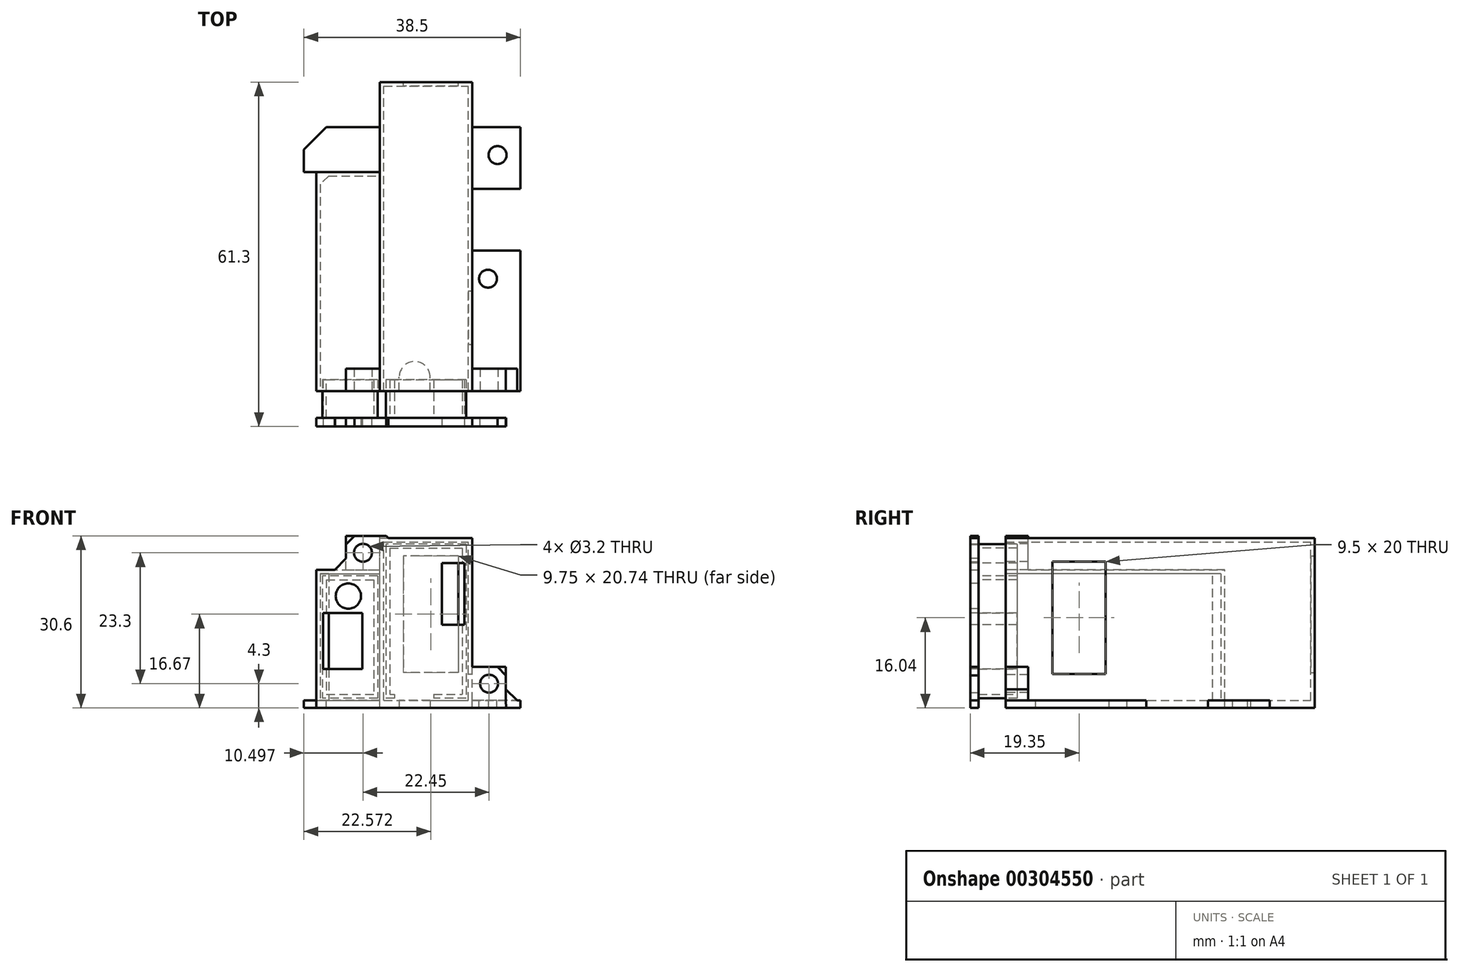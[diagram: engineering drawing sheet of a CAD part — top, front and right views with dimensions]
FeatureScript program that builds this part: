
annotation { "Feature Type Name" : "Feature", "Feature Type Description" : "" }
export const myFeature = defineFeature(function(context is Context, id is Id, definition is map)
    precondition{}
    {
        {
            var Q0;
            Q0=qCreatedBy(makeId("Front.planeOp"),FACE);
            var sketch = newSketch(context, id + "F0", { "sketchPlane" : qUnion([Q0])});
            skLineSegment(sketch, "E0.bottom", {"start": v(-5.75, 0.6) * mm, "end": v(10.7, 0.6) * mm});
            skLineSegment(sketch, "E0.top", {"start": v(-5.75, 30.24) * mm, "end": v(10.7, 30.24) * mm});
            skLineSegment(sketch, "E0.left", {"start": v(-5.75, 0.6) * mm, "end": v(-5.75, 30.24) * mm});
            skLineSegment(sketch, "E0.right", {"start": v(10.7, 0.6) * mm, "end": v(10.7, 30.24) * mm});
            skSolve(sketch);
        }
        {
            var Q0;
            Q0=makeQuery(id+"F0.imprint","IMPRINT",FACE,{"disambiguationData":[TD([[makeQuery(id+"F0.imprint","IMPRINT",EDGE,{"derivedFrom":sQuery(id+"F0.wireOp",EDGE,"E0.bottom")}),1.0]])]});
            extrude(context, id + "F1", {"entities" : qUnion([Q0]), "depth" : 55 * mm});
        }
        {
            var Q0;
            Q0=makeQuery(id+"F1.opExtrude","CAP_FACE",FACE,{"disambiguationData":[OSD([sQuery(id+"F0.wireOp",EDGE,"E0.bottom"),sQuery(id+"F0.wireOp",EDGE,"E0.top"),sQuery(id+"F0.wireOp",EDGE,"E0.left"),sQuery(id+"F0.wireOp",EDGE,"E0.right")])],"isStart":false});
            shell(context, id + "F2", {"entities" : qUnion([Q0]), "thickness" : 0.7 * mm});
        }
        {
            var Q0;
            Q0=makeQuery(id+"F1.opExtrude","CAP_FACE",FACE,{"disambiguationData":[OSD([sQuery(id+"F0.wireOp",EDGE,"E0.bottom"),sQuery(id+"F0.wireOp",EDGE,"E0.top"),sQuery(id+"F0.wireOp",EDGE,"E0.left"),sQuery(id+"F0.wireOp",EDGE,"E0.right")])],"isStart":true});
            var sketch = newSketch(context, id + "F3", { "sketchPlane" : qUnion([Q0])});
            skLineSegment(sketch, "E1.bottom", {"start": v(-8.2, 27.04) * mm, "end": v(1.55, 27.04) * mm});
            skLineSegment(sketch, "E1.top", {"start": v(-8.2, 6.3) * mm, "end": v(1.55, 6.3) * mm});
            skLineSegment(sketch, "E1.left", {"start": v(-8.2, 27.04) * mm, "end": v(-8.2, 6.3) * mm});
            skLineSegment(sketch, "E1.right", {"start": v(1.55, 27.04) * mm, "end": v(1.55, 6.3) * mm});
            skLineSegment(sketch, "E2.0.0", {"start": v(-10, 29.54) * mm, "end": v(5.05, 29.54) * mm});
            skLineSegment(sketch, "E2.0.1", {"start": v(5.05, 29.54) * mm, "end": v(5.05, 1.3) * mm});
            skLineSegment(sketch, "E2.0.2", {"start": v(5.05, 1.3) * mm, "end": v(-10, 1.3) * mm});
            skLineSegment(sketch, "E2.0.3", {"start": v(-10, 1.3) * mm, "end": v(-10, 29.54) * mm});
            skSolve(sketch);
        }
        {
            var Q0;
            Q0=makeQuery(id+"F3.imprint","IMPRINT",FACE,{"disambiguationData":[TD([[makeQuery(id+"F3.imprint","IMPRINT",EDGE,{"derivedFrom":sQuery(id+"F3.wireOp",EDGE,"E1.bottom")}),-1.0]])]});
            extrude(context, id + "F4", {"entities" : qUnion([Q0]), "operationType" : NewBodyOperationType.REMOVE, "endBound" : BoundingType.UP_TO_NEXT, "oppositeDirection" : true, "depth" : 25 * mm});
        }
        {
            var Q0;
            Q0=makeQuery(id+"F2.opShell","OFFSET_FACE",FACE,{"disambiguationData":[OSD([sQuery(id+"F0.wireOp",EDGE,"E0.left")])]});
            var sketch = newSketch(context, id + "F5", { "sketchPlane" : qUnion([Q0])});
            skLineSegment(sketch, "E3.bottom", {"start": v(-16, 24.6) * mm, "end": v(-55, 24.6) * mm});
            skLineSegment(sketch, "E3.top", {"start": v(-16, 0.6) * mm, "end": v(-55, 0.6) * mm});
            skLineSegment(sketch, "E3.left", {"start": v(-16, 24.6) * mm, "end": v(-16, 0.6) * mm});
            skLineSegment(sketch, "E3.right", {"start": v(-55, 24.6) * mm, "end": v(-55, 0.6) * mm});
            skSolve(sketch);
        }
        {
            var Q0;
            Q0 = qSketchRegion(id + "F5", true);
            extrude(context, id + "F6", {"entities" : qUnion([Q0]), "oppositeDirection" : true, "depth" : 12 * mm});
        }
        {
            var Q0;
            Q0=makeQuery(id+"F6.opExtrude","SWEPT_FACE",FACE,{"disambiguationData":[OSD([sQuery(id+"F5.wireOp",EDGE,"E3.right")])]});
            shell(context, id + "F7", {"entities" : qUnion([Q0]), "thickness" : 0.7 * mm});
        }
        {
            var Q0;
            Q0=qCreatedBy(makeId("Top.planeOp"),FACE);
            var sketch = newSketch(context, id + "F8", { "sketchPlane" : qUnion([Q0])});
            skLineSegment(sketch, "E4.bottom", {"start": v(-19.25, -55) * mm, "end": v(19.25, -55) * mm});
            skLineSegment(sketch, "E4.top", {"start": v(-19.25, 0) * mm, "end": v(19.25, 0) * mm});
            skLineSegment(sketch, "E4.left", {"start": v(-19.25, -55) * mm, "end": v(-19.25, 0) * mm});
            skLineSegment(sketch, "E4.right", {"start": v(19.25, -55) * mm, "end": v(19.25, 0) * mm});
            skPoint(sketch, "E5.0", {"position": v(-5.75, -55) * mm});
            skSolve(sketch);
        }
        {
            var Q0;
            Q0=makeQuery(id+"F8.imprint","IMPRINT",FACE,{"disambiguationData":[TD([[makeQuery(id+"F8.imprint","IMPRINT",EDGE,{"derivedFrom":sQuery(id+"F8.wireOp",EDGE,"E4.bottom")}),1.0]])]});
            extrude(context, id + "F9", {"entities" : qUnion([Q0]), "depth" : 1.3 * mm});
        }
        {
            var Q0;
            Q0=makeQuery(id+"F9.opExtrude","CAP_FACE",FACE,{"disambiguationData":[OSD([sQuery(id+"F8.wireOp",EDGE,"E4.bottom"),sQuery(id+"F8.wireOp",EDGE,"E4.top"),sQuery(id+"F8.wireOp",EDGE,"E4.left"),sQuery(id+"F8.wireOp",EDGE,"E4.right")])],"isStart":false});
            var sketch = newSketch(context, id + "F10", { "sketchPlane" : qUnion([Q0])});
            skCircle(sketch, "E6", {"center": v(15.2, -13) * mm, "radius": 1.6 * mm});
            skCircle(sketch, "E7", {"center": v(13.5, -35) * mm, "radius": 1.6 * mm});
            skSolve(sketch);
        }
        {
            var Q0;
            Q0 = qSketchRegion(id + "F10", true);
            var Q1;
            Q1=makeQuery(id+"F9.opExtrude","CAP_FACE",FACE,{"disambiguationData":[OSD([sQuery(id+"F8.wireOp",EDGE,"E4.bottom"),sQuery(id+"F8.wireOp",EDGE,"E4.top"),sQuery(id+"F8.wireOp",EDGE,"E4.left"),sQuery(id+"F8.wireOp",EDGE,"E4.right")])],"isStart":true});
            extrude(context, id + "F11", {"entities" : qUnion([Q0]), "operationType" : NewBodyOperationType.REMOVE, "endBound" : BoundingType.UP_TO_SURFACE, "oppositeDirection" : true, "endBoundEntityFace" : qUnion([Q1]), "depth" : 25 * mm});
        }
        {
            var Q0;
            Q0=makeQuery(id+"F9.opExtrude","SWEPT_EDGE",EDGE,{"disambiguationData":[OSD([sQuery(id+"F8.wireOp",EDGE,"E4.top"),sQuery(id+"F8.wireOp",EDGE,"E4.left")])]});
            chamfer(context, id + "F12", {"entities" : qUnion([Q0]), "width" : 12 * mm, "tangentPropagation" : true});
        }
        {
            var Q0;
            Q0=makeQuery(id+"F9.opExtrude","SWEPT_EDGE",EDGE,{"disambiguationData":[OSD([sQuery(id+"F8.wireOp",EDGE,"E4.top"),sQuery(id+"F8.wireOp",EDGE,"E4.right")])]});
            chamfer(context, id + "F13", {"entities" : qUnion([Q0]), "width" : 8 * mm, "tangentPropagation" : true});
        }
        {
            var Q0;
            Q0=makeQuery(id+"F6.opExtrude","SWEPT_FACE",FACE,{"disambiguationData":[OSD([sQuery(id+"F5.wireOp",EDGE,"E3.right")])]});
            var sketch = newSketch(context, id + "F14", { "sketchPlane" : qUnion([Q0])});
            skLineSegment(sketch, "E8.bottom", {"start": v(-11.75, 24.6) * mm, "end": v(-5.75, 24.6) * mm});
            skLineSegment(sketch, "E8.top", {"start": v(-11.75, 30.6) * mm, "end": v(-5.75, 30.6) * mm});
            skLineSegment(sketch, "E8.left", {"start": v(-11.75, 24.6) * mm, "end": v(-11.75, 30.6) * mm});
            skLineSegment(sketch, "E8.right", {"start": v(-5.75, 24.6) * mm, "end": v(-5.75, 30.6) * mm});
            skPoint(sketch, "E9", {"position": v(-8.75, 27.6) * mm});
            skLineSegment(sketch, "E10", {"start": v(-11.75, 27.6) * mm, "end": v(-5.75, 27.6) * mm});
            skPoint(sketch, "E11.0", {"position": v(10.7, 0.6) * mm});
            skLineSegment(sketch, "E12.bottom", {"start": v(10.7, 1.3) * mm, "end": v(16.7, 1.3) * mm});
            skLineSegment(sketch, "E12.top", {"start": v(10.7, 7.3) * mm, "end": v(16.7, 7.3) * mm});
            skLineSegment(sketch, "E12.left", {"start": v(10.7, 1.3) * mm, "end": v(10.7, 7.3) * mm});
            skLineSegment(sketch, "E12.right", {"start": v(16.7, 1.3) * mm, "end": v(16.7, 7.3) * mm});
            skLineSegment(sketch, "E13", {"start": v(10.7, 4.3) * mm, "end": v(16.7, 4.3) * mm});
            skPoint(sketch, "E14", {"position": v(13.7, 4.3) * mm});
            skCircle(sketch, "E15", {"center": v(-8.75, 27.6) * mm, "radius": 1.6 * mm});
            skCircle(sketch, "E16", {"center": v(13.7, 4.3) * mm, "radius": 1.6 * mm});
            skSolve(sketch);
        }
        {
            var Q0;
            Q0=makeQuery(id+"F14.imprint","IMPRINT",FACE,{"disambiguationData":[TD([[makeQuery(id+"F14.imprint","IMPRINT",EDGE,{"derivedFrom":sQuery(id+"F14.wireOp",EDGE,"E8.bottom")}),1.0]])]});
            var Q1;
            {var subQ0=sQuery(id+"F14.wireOp",EDGE,"E8.top");Q1=makeQuery(id+"F14.imprint","IMPRINT",FACE,{"disambiguationData":[TD([[makeQuery(id+"F14.imprint","IMPRINT",EDGE,{"derivedFrom":subQ0}),-1.0]])]});}
            var Q2;
            {var subQ0=sQuery(id+"F14.wireOp",EDGE,"E12.top");Q2=makeQuery(id+"F14.imprint","IMPRINT",FACE,{"disambiguationData":[TD([[makeQuery(id+"F14.imprint","IMPRINT",EDGE,{"derivedFrom":subQ0}),-1.0]])]});}
            var Q3;
            {var subQ0=sQuery(id+"F14.wireOp",EDGE,"E12.bottom");Q3=makeQuery(id+"F14.imprint","IMPRINT",FACE,{"disambiguationData":[TD([[makeQuery(id+"F14.imprint","IMPRINT",EDGE,{"derivedFrom":subQ0}),1.0]])]});}
            extrude(context, id + "F15", {"entities" : qUnion([Q0, Q1, Q2, Q3]), "oppositeDirection" : true, "depth" : 4 * mm});
        }
        {
            var Q0;
            Q0=makeQuery(id+"F15.opExtrude","CAP_FACE",FACE,{"disambiguationData":[OSD([sQuery(id+"F14.wireOp",EDGE,"E8.bottom"),sQuery(id+"F14.wireOp",EDGE,"E8.top"),sQuery(id+"F14.wireOp",EDGE,"E8.left"),sQuery(id+"F14.wireOp",EDGE,"E8.right")])],"isStart":true});
            var sketch = newSketch(context, id + "F16", { "sketchPlane" : qUnion([Q0])});
            skPoint(sketch, "E17.0", {"position": v(-5.75, 30.24) * mm});
            skPoint(sketch, "E18.0", {"position": v(10.7, 30.24) * mm});
            skPoint(sketch, "E19.0", {"position": v(10.7, 0.6) * mm});
            skPoint(sketch, "E20.0", {"position": v(-17.05, 0.6) * mm});
            skPoint(sketch, "E21.0", {"position": v(-17.05, 24.6) * mm});
            skPoint(sketch, "E22.0", {"position": v(-11.75, 24.6) * mm});
            skPoint(sketch, "E23.0", {"position": v(-11.75, 30.6) * mm});
            skPoint(sketch, "E24.0", {"position": v(-5.75, 30.6) * mm});
            skLineSegment(sketch, "E25", {"start": v(-17.05, 0) * mm, "end": v(-17.05, 24.6) * mm});
            skLineSegment(sketch, "E26", {"start": v(-17.05, 24.6) * mm, "end": v(-11.75, 24.6) * mm});
            skLineSegment(sketch, "E27", {"start": v(-11.75, 24.6) * mm, "end": v(-11.75, 30.6) * mm});
            skLineSegment(sketch, "E28", {"start": v(-11.75, 30.6) * mm, "end": v(-5.75, 30.6) * mm});
            skLineSegment(sketch, "E29", {"start": v(-5.75, 30.6) * mm, "end": v(-5.75, 30.24) * mm});
            skLineSegment(sketch, "E30", {"start": v(-5.75, 30.24) * mm, "end": v(10.7, 30.24) * mm});
            skLineSegment(sketch, "E31", {"start": v(16.72, 0) * mm, "end": v(-17.05, 0) * mm});
            skPoint(sketch, "E32.0", {"position": v(10.7, 7.3) * mm});
            skPoint(sketch, "E33.0", {"position": v(16.7, 1.3) * mm});
            skLineSegment(sketch, "E34", {"start": v(10.7, 30.24) * mm, "end": v(10.7, 7.3) * mm});
            skLineSegment(sketch, "E35", {"start": v(16.72, 0) * mm, "end": v(16.7, 1.3) * mm});
            skLineSegment(sketch, "E36", {"start": v(16.7, 1.3) * mm, "end": v(10.7, 1.3) * mm});
            skLineSegment(sketch, "E37", {"start": v(10.7, 1.3) * mm, "end": v(10.7, 7.3) * mm});
            skSolve(sketch);
        }
        {
            var Q0;
            Q0=makeQuery(id+"F16.imprint","IMPRINT",FACE,{"disambiguationData":[TD([[makeQuery(id+"F16.imprint","IMPRINT",EDGE,{"derivedFrom":sQuery(id+"F16.wireOp",EDGE,"E25")}),-1.0]])]});
            var Q1;
            Q1=makeQuery(id+"F16.imprint","IMPRINT",FACE,{"disambiguationData":[TD([[makeQuery(id+"F16.imprint","IMPRINT",EDGE,{"derivedFrom":sQuery(id+"F16.wireOp",EDGE,"E27")}),-1.0]])]});
            var Q2;
            Q2=makeQuery(id+"F15.opExtrude","CAP_FACE",FACE,{"disambiguationData":[OSD([sQuery(id+"F14.wireOp",EDGE,"E12.bottom"),sQuery(id+"F14.wireOp",EDGE,"E12.top"),sQuery(id+"F14.wireOp",EDGE,"E12.left"),sQuery(id+"F14.wireOp",EDGE,"E12.right"),sQuery(id+"F14.wireOp",EDGE,"E16")])],"isStart":true});
            extrude(context, id + "F17", {"entities" : qUnion([Q0, Q1, Q2]), "depth" : 1.5 * mm});
        }
        {
            var Q0;
            Q0=makeQuery(id+"F17.opExtrude","CAP_FACE",FACE,{"disambiguationData":[OSD([sQuery(id+"F16.wireOp",EDGE,"E25"),sQuery(id+"F16.wireOp",EDGE,"E26"),sQuery(id+"F16.wireOp",EDGE,"E27"),sQuery(id+"F16.wireOp",EDGE,"E28"),sQuery(id+"F16.wireOp",EDGE,"E29"),sQuery(id+"F16.wireOp",EDGE,"E30"),sQuery(id+"F16.wireOp",EDGE,"dLR5ZEAd-W9p6-nn1V-uw1r-p6ehXEuAr7GT"),sQuery(id+"F16.wireOp",EDGE,"E31")])],"isStart":true});
            var sketch = newSketch(context, id + "F18", { "sketchPlane" : qUnion([Q0])});
            skPoint(sketch, "E38.0", {"position": v(16.35, 23.9) * mm});
            skPoint(sketch, "E39.0", {"position": v(5.75, 23.9) * mm});
            skPoint(sketch, "E40.0", {"position": v(5.75, 1.3) * mm});
            skPoint(sketch, "E41.0", {"position": v(16.35, 1.3) * mm});
            skPoint(sketch, "E42.0", {"position": v(5.05, 1.3) * mm});
            skPoint(sketch, "E43.0", {"position": v(-10, 1.3) * mm});
            skPoint(sketch, "E44.0", {"position": v(5.05, 29.54) * mm});
            skPoint(sketch, "E45.0", {"position": v(-10, 29.54) * mm});
            skLineSegment(sketch, "E46.bottom", {"start": v(-9.6, 29.14) * mm, "end": v(4.65, 29.14) * mm});
            skLineSegment(sketch, "E46.top", {"start": v(-9.6, 1.7) * mm, "end": v(4.65, 1.7) * mm});
            skLineSegment(sketch, "E46.left", {"start": v(-9.6, 29.14) * mm, "end": v(-9.6, 1.7) * mm});
            skLineSegment(sketch, "E46.right", {"start": v(4.65, 29.14) * mm, "end": v(4.65, 1.7) * mm});
            skLineSegment(sketch, "E47.bottom", {"start": v(6.15, 23.5) * mm, "end": v(15.95, 23.5) * mm});
            skLineSegment(sketch, "E47.top", {"start": v(6.15, 1.7) * mm, "end": v(15.95, 1.7) * mm});
            skLineSegment(sketch, "E47.left", {"start": v(6.15, 23.5) * mm, "end": v(6.15, 1.7) * mm});
            skLineSegment(sketch, "E47.right", {"start": v(15.95, 23.5) * mm, "end": v(15.95, 1.7) * mm});
            skLineSegment(sketch, "E48.bottom", {"start": v(15.25, 22.8) * mm, "end": v(6.85, 22.8) * mm});
            skLineSegment(sketch, "E48.top", {"start": v(15.25, 2.4) * mm, "end": v(6.85, 2.4) * mm});
            skLineSegment(sketch, "E48.left", {"start": v(15.25, 22.8) * mm, "end": v(15.25, 2.4) * mm});
            skLineSegment(sketch, "E48.right", {"start": v(6.85, 22.8) * mm, "end": v(6.85, 2.4) * mm});
            skLineSegment(sketch, "E49.bottom", {"start": v(3.95, 28.44) * mm, "end": v(-8.9, 28.44) * mm});
            skLineSegment(sketch, "E49.top", {"start": v(3.95, 2.4) * mm, "end": v(-8.9, 2.4) * mm});
            skLineSegment(sketch, "E49.left", {"start": v(3.95, 28.44) * mm, "end": v(3.95, 2.4) * mm});
            skLineSegment(sketch, "E49.right", {"start": v(-8.9, 28.44) * mm, "end": v(-8.9, 2.4) * mm});
            skSolve(sketch);
        }
        {
            var Q0;
            Q0=makeQuery(id+"F18.imprint","IMPRINT",FACE,{"disambiguationData":[TD([[makeQuery(id+"F18.imprint","IMPRINT",EDGE,{"derivedFrom":sQuery(id+"F18.wireOp",EDGE,"E46.bottom")}),-1.0]])]});
            var Q1;
            Q1=makeQuery(id+"F18.imprint","IMPRINT",FACE,{"disambiguationData":[TD([[makeQuery(id+"F18.imprint","IMPRINT",EDGE,{"derivedFrom":sQuery(id+"F18.wireOp",EDGE,"E47.bottom")}),-1.0]])]});
            extrude(context, id + "F19", {"entities" : qUnion([Q0, Q1]), "operationType" : NewBodyOperationType.ADD, "depth" : 6.8 * mm});
        }
        {
            var Q0;
            Q0=makeQuery(id+"F17.opExtrude","SWEPT_BODY",BODY,{"disambiguationData":[OSD([sQuery(id+"F14.wireOp",EDGE,"E12.bottom"),sQuery(id+"F14.wireOp",EDGE,"E12.top"),sQuery(id+"F14.wireOp",EDGE,"E12.left"),sQuery(id+"F14.wireOp",EDGE,"E12.right"),sQuery(id+"F14.wireOp",EDGE,"E16")])]});
            var Q1;
            Q1=makeQuery(id+"F17.opExtrude","SWEPT_BODY",BODY,{"disambiguationData":[OSD([sQuery(id+"F14.wireOp",EDGE,"E15"),sQuery(id+"F16.wireOp",EDGE,"E25"),sQuery(id+"F16.wireOp",EDGE,"E26"),sQuery(id+"F16.wireOp",EDGE,"E27"),sQuery(id+"F16.wireOp",EDGE,"E28"),sQuery(id+"F16.wireOp",EDGE,"E29"),sQuery(id+"F16.wireOp",EDGE,"E30"),sQuery(id+"F16.wireOp",EDGE,"E31"),sQuery(id+"F16.wireOp",EDGE,"E34"),sQuery(id+"F16.wireOp",EDGE,"QFazLDCa-6nAL-WsGP-17c7-o35cEx2jxHVR"),sQuery(id+"F16.wireOp",EDGE,"E35"),sQuery(id+"F16.wireOp",EDGE,"E36"),sQuery(id+"F16.wireOp",EDGE,"E37")])]});
            booleanBodies(context, id + "F20", {"operationType" : BooleanOperationType.UNION, "tools" : qUnion([Q0, Q1])});
        }
        {
            var Q0;
            Q0=makeQuery(id+"F17.opExtrude","SWEPT_BODY",BODY,{"disambiguationData":[OSD([sQuery(id+"F14.wireOp",EDGE,"E12.bottom"),sQuery(id+"F14.wireOp",EDGE,"E12.top"),sQuery(id+"F14.wireOp",EDGE,"E12.left"),sQuery(id+"F14.wireOp",EDGE,"E12.right"),sQuery(id+"F14.wireOp",EDGE,"E16")])]});
            transform(context, id + "F21", {"entities" : qUnion([Q0]), "transformType" : TransformType.TRANSLATION_3D, "dx" : 0 * mm, "dy" : -20 * mm, "dz" : 0 * mm, "makeCopy" : false});
        }
        {
            var Q0;
            Q0=makeQuery(id+"F20.opBoolean","MERGE",FACE,{"derivedFrom":[makeQuery(id+"F17.opExtrude","CAP_FACE",FACE,{"disambiguationData":[OSD([sQuery(id+"F14.wireOp",EDGE,"E12.bottom"),sQuery(id+"F14.wireOp",EDGE,"E12.top"),sQuery(id+"F14.wireOp",EDGE,"E12.left"),sQuery(id+"F14.wireOp",EDGE,"E12.right"),sQuery(id+"F14.wireOp",EDGE,"E16")])],"isStart":false}),makeQuery(id+"F17.opExtrude","CAP_FACE",FACE,{"disambiguationData":[OSD([sQuery(id+"F14.wireOp",EDGE,"E15"),sQuery(id+"F16.wireOp",EDGE,"E25"),sQuery(id+"F16.wireOp",EDGE,"E26"),sQuery(id+"F16.wireOp",EDGE,"E27"),sQuery(id+"F16.wireOp",EDGE,"E28"),sQuery(id+"F16.wireOp",EDGE,"E29"),sQuery(id+"F16.wireOp",EDGE,"E30"),sQuery(id+"F16.wireOp",EDGE,"E31"),sQuery(id+"F16.wireOp",EDGE,"E34"),sQuery(id+"F16.wireOp",EDGE,"QFazLDCa-6nAL-WsGP-17c7-o35cEx2jxHVR"),sQuery(id+"F16.wireOp",EDGE,"E35"),sQuery(id+"F16.wireOp",EDGE,"E36"),sQuery(id+"F16.wireOp",EDGE,"E37")])],"isStart":false})]});
            var sketch = newSketch(context, id + "F22", { "sketchPlane" : qUnion([Q0])});
            skLineSegment(sketch, "E50.bottom", {"start": v(-15.85, 6.9) * mm, "end": v(-8.85, 6.9) * mm});
            skLineSegment(sketch, "E50.top", {"start": v(-15.85, 16.9) * mm, "end": v(-8.85, 16.9) * mm});
            skLineSegment(sketch, "E50.left", {"start": v(-15.85, 6.9) * mm, "end": v(-15.85, 16.9) * mm});
            skLineSegment(sketch, "E50.right", {"start": v(-8.85, 6.9) * mm, "end": v(-8.85, 16.9) * mm});
            skCircle(sketch, "E51", {"center": v(-11.35, 19.9) * mm, "radius": 2.25 * mm});
            skPoint(sketch, "E52.0", {"position": v(-16.35, 23.9) * mm});
            skPoint(sketch, "E53.0", {"position": v(-16.35, 1.3) * mm});
            skPoint(sketch, "E54.0", {"position": v(-5.75, 23.9) * mm});
            skPoint(sketch, "E55.0", {"position": v(-5.05, 29.54) * mm});
            skPoint(sketch, "E56.0", {"position": v(10, 29.54) * mm});
            skPoint(sketch, "E57.0", {"position": v(-5.75, 1.3) * mm});
            skPoint(sketch, "E58.0", {"position": v(-5.05, 1.3) * mm});
            skPoint(sketch, "E59.0", {"position": v(10, 1.3) * mm});
            skPoint(sketch, "E60", {"position": v(-12.35, 16.9) * mm});
            skLineSegment(sketch, "E61.bottom", {"start": v(9.3, 25.79) * mm, "end": v(5.3, 25.79) * mm});
            skLineSegment(sketch, "E61.top", {"start": v(9.3, 14.79) * mm, "end": v(5.3, 14.79) * mm});
            skLineSegment(sketch, "E61.left", {"start": v(9.3, 25.79) * mm, "end": v(9.3, 14.79) * mm});
            skLineSegment(sketch, "E61.right", {"start": v(5.3, 25.79) * mm, "end": v(5.3, 14.79) * mm});
            skSolve(sketch);
        }
        {
            var Q0;
            Q0=makeQuery(id+"F22.imprint","IMPRINT",FACE,{"disambiguationData":[TD([[makeQuery(id+"F22.imprint","IMPRINT",EDGE,{"derivedFrom":sQuery(id+"F22.wireOp",EDGE,"E51")}),1.0]])]});
            var Q1;
            Q1=makeQuery(id+"F22.imprint","IMPRINT",FACE,{"disambiguationData":[TD([[makeQuery(id+"F22.imprint","IMPRINT",EDGE,{"derivedFrom":sQuery(id+"F22.wireOp",EDGE,"E50.bottom")}),1.0]])]});
            var Q2;
            Q2=makeQuery(id+"F22.imprint","IMPRINT",FACE,{"disambiguationData":[TD([[makeQuery(id+"F22.imprint","IMPRINT",EDGE,{"derivedFrom":sQuery(id+"F22.wireOp",EDGE,"E61.bottom")}),1.0]])]});
            extrude(context, id + "F23", {"entities" : qUnion([Q0, Q1, Q2]), "operationType" : NewBodyOperationType.REMOVE, "endBound" : BoundingType.UP_TO_NEXT, "oppositeDirection" : true, "depth" : 25 * mm});
        }
        {
            var Q0;
            Q0=makeQuery(id+"F1.opExtrude","SWEPT_FACE",FACE,{"disambiguationData":[OSD([sQuery(id+"F0.wireOp",EDGE,"E0.right")])]});
            var sketch = newSketch(context, id + "F24", { "sketchPlane" : qUnion([Q0])});
            skLineSegment(sketch, "E62.bottom", {"start": v(-37.2, 6.04) * mm, "end": v(-46.7, 6.04) * mm});
            skLineSegment(sketch, "E62.top", {"start": v(-37.2, 26.04) * mm, "end": v(-46.7, 26.04) * mm});
            skLineSegment(sketch, "E62.left", {"start": v(-37.2, 6.04) * mm, "end": v(-37.2, 26.04) * mm});
            skLineSegment(sketch, "E62.right", {"start": v(-46.7, 6.04) * mm, "end": v(-46.7, 26.04) * mm});
            skSolve(sketch);
        }
        {
            var Q0;
            Q0=makeQuery(id+"F24.imprint","IMPRINT",FACE,{"disambiguationData":[TD([[makeQuery(id+"F24.imprint","IMPRINT",EDGE,{"derivedFrom":sQuery(id+"F24.wireOp",EDGE,"E62.bottom")}),-1.0]])]});
            extrude(context, id + "F25", {"entities" : qUnion([Q0]), "operationType" : NewBodyOperationType.REMOVE, "endBound" : BoundingType.UP_TO_NEXT, "oppositeDirection" : true, "depth" : 25 * mm});
        }
        {
            var Q0;
            Q0=makeQuery(id+"F17.opExtrude","SWEPT_BODY",BODY,{"disambiguationData":[OSD([sQuery(id+"F14.wireOp",EDGE,"E12.bottom"),sQuery(id+"F14.wireOp",EDGE,"E12.top"),sQuery(id+"F14.wireOp",EDGE,"E12.left"),sQuery(id+"F14.wireOp",EDGE,"E12.right"),sQuery(id+"F14.wireOp",EDGE,"E16")])]});
            transform(context, id + "F26", {"entities" : qUnion([Q0]), "transformType" : TransformType.TRANSLATION_3D, "dx" : 0 * mm, "dy" : 15.2 * mm, "dz" : 0 * mm, "makeCopy" : false});
        }
        {
            var Q0;
            Q0=makeQuery(id+"F9.opExtrude","CAP_FACE",FACE,{"disambiguationData":[OSD([sQuery(id+"F8.wireOp",EDGE,"E4.bottom"),sQuery(id+"F8.wireOp",EDGE,"E4.top"),sQuery(id+"F8.wireOp",EDGE,"E4.left"),sQuery(id+"F8.wireOp",EDGE,"E4.right")])],"isStart":true});
            var sketch = newSketch(context, id + "F27", { "sketchPlane" : qUnion([Q0])});
            skLineSegment(sketch, "E63", {"start": v(-2.3, 55) * mm, "end": v(3.2, 55) * mm});
            skLineSegment(sketch, "E64", {"start": v(3.2, 55) * mm, "end": v(3.2, 52.5) * mm});
            skLineSegment(sketch, "E65", {"start": v(-2.3, 55) * mm, "end": v(-2.3, 52.5) * mm});
            skArc(sketch, "E66", {"start": v(-2.3, 52.5) * mm, "mid": v(0.45, 49.75) * mm, "end": v(3.2, 52.5) * mm});
            skPoint(sketch, "E67.0", {"position": v(-5.05, 55) * mm});
            skPoint(sketch, "E68", {"position": v(0.45, 55) * mm});
            skSolve(sketch);
        }
        {
            var Q0;
            Q0=makeQuery(id+"F27.imprint","IMPRINT",FACE,{"disambiguationData":[TD([[makeQuery(id+"F27.imprint","IMPRINT",EDGE,{"derivedFrom":sQuery(id+"F27.wireOp",EDGE,"E63")}),-1.0]])]});
            extrude(context, id + "F28", {"entities" : qUnion([Q0]), "oppositeDirection" : true, "depth" : 5 * mm});
        }
        {
            var Q0;
            Q0=makeQuery(id+"F1.opExtrude","SWEPT_BODY",BODY,{"disambiguationData":[OSD([sQuery(id+"F0.wireOp",EDGE,"E0.bottom"),sQuery(id+"F0.wireOp",EDGE,"E0.top"),sQuery(id+"F0.wireOp",EDGE,"E0.left"),sQuery(id+"F0.wireOp",EDGE,"E0.right")])]});
            var Q1;
            Q1=makeQuery(id+"F6.opExtrude","SWEPT_BODY",BODY,{"disambiguationData":[OSD([sQuery(id+"F5.wireOp",EDGE,"E3.bottom"),sQuery(id+"F5.wireOp",EDGE,"E3.top"),sQuery(id+"F5.wireOp",EDGE,"E3.left"),sQuery(id+"F5.wireOp",EDGE,"E3.right")])]});
            var Q2;
            Q2=makeQuery(id+"F9.opExtrude","SWEPT_BODY",BODY,{"disambiguationData":[OSD([sQuery(id+"F8.wireOp",EDGE,"E4.bottom"),sQuery(id+"F8.wireOp",EDGE,"E4.top"),sQuery(id+"F8.wireOp",EDGE,"E4.left"),sQuery(id+"F8.wireOp",EDGE,"E4.right")])]});
            var Q3;
            Q3=makeQuery(id+"F15.opExtrude","SWEPT_BODY",BODY,{"disambiguationData":[OSD([sQuery(id+"F14.wireOp",EDGE,"E8.bottom"),sQuery(id+"F14.wireOp",EDGE,"E8.top"),sQuery(id+"F14.wireOp",EDGE,"E8.left"),sQuery(id+"F14.wireOp",EDGE,"E8.right"),sQuery(id+"F14.wireOp",EDGE,"E15")])]});
            var Q4;
            Q4=makeQuery(id+"F15.opExtrude","SWEPT_BODY",BODY,{"disambiguationData":[OSD([sQuery(id+"F14.wireOp",EDGE,"E12.bottom"),sQuery(id+"F14.wireOp",EDGE,"E12.top"),sQuery(id+"F14.wireOp",EDGE,"E12.left"),sQuery(id+"F14.wireOp",EDGE,"E12.right"),sQuery(id+"F14.wireOp",EDGE,"E16")])]});
            booleanBodies(context, id + "F29", {"operationType" : BooleanOperationType.UNION, "tools" : qUnion([Q0, Q1, Q2, Q3, Q4])});
        }
        {
            var Q0;
            Q0=makeQuery(id+"F28.opExtrude","SWEPT_BODY",BODY,{"disambiguationData":[OSD([sQuery(id+"F27.wireOp",EDGE,"E63"),sQuery(id+"F27.wireOp",EDGE,"E64"),sQuery(id+"F27.wireOp",EDGE,"E65"),sQuery(id+"F27.wireOp",EDGE,"E66")])]});
            var Q1;
            Q1=makeQuery(id+"F1.opExtrude","SWEPT_BODY",BODY,{"disambiguationData":[OSD([sQuery(id+"F0.wireOp",EDGE,"E0.bottom"),sQuery(id+"F0.wireOp",EDGE,"E0.top"),sQuery(id+"F0.wireOp",EDGE,"E0.left"),sQuery(id+"F0.wireOp",EDGE,"E0.right")])]});
            booleanBodies(context, id + "F30", {"operationType" : BooleanOperationType.SUBTRACTION, "tools" : qUnion([Q0]), "targets" : qUnion([Q1])});
        }
        {
            var Q0;
            Q0=makeQuery(id+"F19.opExtrude","SWEPT_FACE",FACE,{"disambiguationData":[OSD([sQuery(id+"F18.wireOp",EDGE,"E46.top")])]});
            var sketch = newSketch(context, id + "F31", { "sketchPlane" : qUnion([Q0])});
            skLineSegment(sketch, "E69.bottom", {"start": v(-3.15, 53) * mm, "end": v(3.85, 53) * mm});
            skLineSegment(sketch, "E69.top", {"start": v(-3.15, 59.8) * mm, "end": v(3.85, 59.8) * mm});
            skLineSegment(sketch, "E69.left", {"start": v(-3.15, 53) * mm, "end": v(-3.15, 59.8) * mm});
            skLineSegment(sketch, "E69.right", {"start": v(3.85, 53) * mm, "end": v(3.85, 59.8) * mm});
            skSolve(sketch);
        }
        {
            var Q0;
            Q0=makeQuery(id+"F31.imprint","IMPRINT",FACE,{"disambiguationData":[TD([[makeQuery(id+"F31.imprint","IMPRINT",EDGE,{"derivedFrom":sQuery(id+"F31.wireOp",EDGE,"E69.bottom")}),-1.0]])]});
            extrude(context, id + "F32", {"entities" : qUnion([Q0]), "operationType" : NewBodyOperationType.REMOVE, "endBound" : BoundingType.UP_TO_NEXT, "oppositeDirection" : true, "depth" : 25 * mm});
        }
        {
            var Q0;
            Q0=makeQuery(id+"F15.opExtrude","SWEPT_EDGE",EDGE,{"disambiguationData":[OSD([sQuery(id+"F14.wireOp",EDGE,"E12.top"),sQuery(id+"F14.wireOp",EDGE,"E12.left")])]});
            var Q1;
            Q1=makeQuery(id+"F15.opExtrude","SWEPT_EDGE",EDGE,{"disambiguationData":[OSD([sQuery(id+"F14.wireOp",EDGE,"E12.bottom"),sQuery(id+"F14.wireOp",EDGE,"E12.right")])]});
            var Q2;
            Q2=makeQuery(id+"F15.opExtrude","SWEPT_EDGE",EDGE,{"disambiguationData":[OSD([sQuery(id+"F0.wireOp",EDGE,"E0.left"),sQuery(id+"F5.wireOp",EDGE,"E3.bottom"),sQuery(id+"F5.wireOp",EDGE,"E3.right"),sQuery(id+"F14.wireOp",EDGE,"E8.bottom"),sQuery(id+"F14.wireOp",EDGE,"E8.left")])]});
            var Q3;
            Q3=makeQuery(id+"F17.opExtrude","SWEPT_EDGE",EDGE,{"disambiguationData":[OSD([sQuery(id+"F14.wireOp",EDGE,"E12.top"),sQuery(id+"F14.wireOp",EDGE,"E12.left")])]});
            var Q4;
            Q4=makeQuery(id+"F17.opExtrude","SWEPT_EDGE",EDGE,{"disambiguationData":[OSD([sQuery(id+"F14.wireOp",EDGE,"E8.bottom"),sQuery(id+"F16.wireOp",EDGE,"E26"),sQuery(id+"F16.wireOp",EDGE,"E27")])]});
            chamfer(context, id + "F33", {"entities" : qUnion([Q0, Q1, Q2, Q3, Q4]), "width" : 2 * mm, "tangentPropagation" : true});
        }
        {
            var Q0;
            {var subQ0=sQuery(id+"F8.wireOp",EDGE,"E4.right");var subQ1=sQuery(id+"F8.wireOp",EDGE,"E4.top");var subQ7=sQuery(id+"F0.wireOp",EDGE,"E0.right");var subQ11=sQuery(id+"F8.wireOp",EDGE,"E4.bottom");Q0=makeQuery(id+"F29.opBoolean","SPLIT",FACE,{"disambiguationData":[TD([makeQuery(id+"F1.opExtrude","SWEPT_FACE",FACE,{"disambiguationData":[OSD([subQ7])]})])],"derivedFrom":makeQuery(id+"F9.opExtrude","CAP_FACE",FACE,{"disambiguationData":[OSD([subQ11,subQ1,sQuery(id+"F8.wireOp",EDGE,"E4.left"),subQ0])],"isStart":false})});}
            var sketch = newSketch(context, id + "F34", { "sketchPlane" : qUnion([Q0])});
            skLineSegment(sketch, "E70.bottom", {"start": v(19.25, -19) * mm, "end": v(10.7, -19) * mm});
            skLineSegment(sketch, "E70.top", {"start": v(19.25, -30) * mm, "end": v(10.7, -30) * mm});
            skLineSegment(sketch, "E70.left", {"start": v(19.25, -19) * mm, "end": v(19.25, -30) * mm});
            skLineSegment(sketch, "E70.right", {"start": v(10.7, -19) * mm, "end": v(10.7, -30) * mm});
            skLineSegment(sketch, "E71.bottom", {"start": v(19.25, -8) * mm, "end": v(10.7, -8) * mm});
            skLineSegment(sketch, "E71.top", {"start": v(19.25, 0) * mm, "end": v(10.7, 0) * mm});
            skLineSegment(sketch, "E71.left", {"start": v(19.25, -8) * mm, "end": v(19.25, 0) * mm});
            skLineSegment(sketch, "E71.right", {"start": v(10.7, -8) * mm, "end": v(10.7, 0) * mm});
            skLineSegment(sketch, "E72.bottom", {"start": v(-5.75, 0) * mm, "end": v(-19.75, 0) * mm});
            skLineSegment(sketch, "E72.top", {"start": v(-5.75, -8) * mm, "end": v(-19.75, -8) * mm});
            skLineSegment(sketch, "E72.left", {"start": v(-5.75, 0) * mm, "end": v(-5.75, -8) * mm});
            skLineSegment(sketch, "E72.right", {"start": v(-19.75, 0) * mm, "end": v(-19.75, -8) * mm});
            skPoint(sketch, "E73.0", {"position": v(-19.25, -55) * mm});
            skPoint(sketch, "E74.0", {"position": v(-17.05, -16) * mm});
            skLineSegment(sketch, "E75.bottom", {"start": v(-19.25, -55) * mm, "end": v(-17.05, -55) * mm});
            skLineSegment(sketch, "E75.top", {"start": v(-19.25, -16) * mm, "end": v(-17.05, -16) * mm});
            skLineSegment(sketch, "E75.left", {"start": v(-19.25, -55) * mm, "end": v(-19.25, -16) * mm});
            skLineSegment(sketch, "E75.right", {"start": v(-17.05, -55) * mm, "end": v(-17.05, -16) * mm});
            skSolve(sketch);
        }
        {
            var Q0;
            Q0=makeQuery(id+"F34.imprint","IMPRINT",FACE,{"disambiguationData":[TD([[makeQuery(id+"F34.imprint","IMPRINT",EDGE,{"derivedFrom":sQuery(id+"F34.wireOp",EDGE,"E72.bottom")}),1.0]])]});
            var Q1;
            {var subQ4=sQuery(id+"F34.wireOp",EDGE,"E71.left");Q1=makeQuery(id+"F34.imprint","IMPRINT",FACE,{"disambiguationData":[TD([[makeQuery(id+"F34.imprint","IMPRINT",EDGE,{"derivedFrom":subQ4}),1.0]])]});}
            var Q2;
            Q2=makeQuery(id+"F34.imprint","IMPRINT",FACE,{"disambiguationData":[TD([[makeQuery(id+"F34.imprint","IMPRINT",EDGE,{"derivedFrom":sQuery(id+"F34.wireOp",EDGE,"E71.bottom")}),-1.0]])]});
            var Q3;
            Q3=makeQuery(id+"F34.imprint","IMPRINT",FACE,{"disambiguationData":[TD([[makeQuery(id+"F34.imprint","IMPRINT",EDGE,{"derivedFrom":sQuery(id+"F34.wireOp",EDGE,"E70.bottom")}),1.0]])]});
            var Q4;
            Q4=makeQuery(id+"F34.imprint","IMPRINT",FACE,{"disambiguationData":[TD([[makeQuery(id+"F34.imprint","IMPRINT",EDGE,{"derivedFrom":sQuery(id+"F34.wireOp",EDGE,"E75.bottom")}),1.0]])]});
            extrude(context, id + "F35", {"entities" : qUnion([Q0, Q1, Q2, Q3, Q4]), "operationType" : NewBodyOperationType.REMOVE, "endBound" : BoundingType.THROUGH_ALL, "oppositeDirection" : true, "depth" : 25 * mm});
        }
        {
            var Q0;
            {var subQ0=makeQuery(id+"F1.opExtrude","SWEPT_FACE",FACE,{"disambiguationData":[OSD([sQuery(id+"F0.wireOp",EDGE,"E0.left")])]});var subQ1=makeQuery(id+"F9.opExtrude","CAP_FACE",FACE,{"disambiguationData":[OSD([sQuery(id+"F8.wireOp",EDGE,"E4.bottom"),sQuery(id+"F8.wireOp",EDGE,"E4.top"),sQuery(id+"F8.wireOp",EDGE,"E4.left"),sQuery(id+"F8.wireOp",EDGE,"E4.right")])],"isStart":false});Q0=makeQuery(id+"F29.opBoolean","INTERSECT",EDGE,{"disambiguationData":[topologyDisambiguationEdgeConnected([subQ1])],"derivedFrom":[subQ0,subQ1]});}
            var Q1;
            Q1=makeQuery(id+"F35.boolean.opBoolean","COPY",EDGE,{"derivedFrom":makeQuery(id+"F35.opExtrude","SWEPT_EDGE",EDGE,{"disambiguationData":[OSD([sQuery(id+"F34.wireOp",EDGE,"E75.top"),sQuery(id+"F34.wireOp",EDGE,"E75.left")])]})});
            var Q2;
            Q2=makeQuery(id+"F35.boolean.opBoolean","COPY",EDGE,{"derivedFrom":makeQuery(id+"F35.opExtrude","SWEPT_EDGE",EDGE,{"disambiguationData":[OSD([sQuery(id+"F0.wireOp",EDGE,"E0.right"),sQuery(id+"F8.wireOp",EDGE,"E4.bottom"),sQuery(id+"F8.wireOp",EDGE,"E4.top"),sQuery(id+"F8.wireOp",EDGE,"E4.left"),sQuery(id+"F8.wireOp",EDGE,"E4.right"),sQuery(id+"F34.wireOp",EDGE,"E71.bottom"),sQuery(id+"F34.wireOp",EDGE,"E71.right")])]})});
            var Q3;
            {var subQ0=sQuery(id+"F8.wireOp",EDGE,"E4.right");var subQ1=sQuery(id+"F8.wireOp",EDGE,"E4.top");Q3=makeQuery(id+"F35.boolean.opBoolean","MERGE",EDGE,{"derivedFrom":[makeQuery(id+"F13.opChamfer","BLEND_EDGE",EDGE,{"blendedFrom":[makeQuery(id+"F9.opExtrude","SWEPT_EDGE",EDGE,{"disambiguationData":[OSD([subQ1,subQ0])]}),makeQuery(id+"F9.opExtrude","SWEPT_FACE",FACE,{"disambiguationData":[OSD([subQ0])]})],"blendedInto":[makeQuery(id+"F9.opExtrude","SWEPT_FACE",FACE,{"disambiguationData":[OSD([subQ0])]})]}),makeQuery(id+"F35.opExtrude","SWEPT_EDGE",EDGE,{"disambiguationData":[OSD([sQuery(id+"F8.wireOp",EDGE,"E4.bottom"),subQ1,sQuery(id+"F8.wireOp",EDGE,"E4.left"),subQ0,sQuery(id+"F34.wireOp",EDGE,"E71.bottom"),sQuery(id+"F34.wireOp",EDGE,"E71.left")])]})]});}
            var Q4;
            Q4=makeQuery(id+"F35.boolean.opBoolean","COPY",EDGE,{"derivedFrom":makeQuery(id+"F35.opExtrude","SWEPT_EDGE",EDGE,{"disambiguationData":[OSD([sQuery(id+"F8.wireOp",EDGE,"E4.right"),sQuery(id+"F34.wireOp",EDGE,"E70.bottom"),sQuery(id+"F34.wireOp",EDGE,"E70.left")])]})});
            var Q5;
            Q5=makeQuery(id+"F35.boolean.opBoolean","COPY",EDGE,{"derivedFrom":makeQuery(id+"F35.opExtrude","SWEPT_EDGE",EDGE,{"disambiguationData":[OSD([sQuery(id+"F0.wireOp",EDGE,"E0.right"),sQuery(id+"F8.wireOp",EDGE,"E4.bottom"),sQuery(id+"F8.wireOp",EDGE,"E4.top"),sQuery(id+"F8.wireOp",EDGE,"E4.left"),sQuery(id+"F8.wireOp",EDGE,"E4.right"),sQuery(id+"F34.wireOp",EDGE,"E70.bottom"),sQuery(id+"F34.wireOp",EDGE,"E70.right")])]})});
            var Q6;
            Q6=makeQuery(id+"F35.boolean.opBoolean","COPY",EDGE,{"derivedFrom":makeQuery(id+"F35.opExtrude","SWEPT_EDGE",EDGE,{"disambiguationData":[OSD([sQuery(id+"F0.wireOp",EDGE,"E0.right"),sQuery(id+"F8.wireOp",EDGE,"E4.bottom"),sQuery(id+"F8.wireOp",EDGE,"E4.top"),sQuery(id+"F8.wireOp",EDGE,"E4.left"),sQuery(id+"F8.wireOp",EDGE,"E4.right"),sQuery(id+"F34.wireOp",EDGE,"E70.top"),sQuery(id+"F34.wireOp",EDGE,"E70.right")])]})});
            var Q7;
            Q7=makeQuery(id+"F35.boolean.opBoolean","COPY",EDGE,{"derivedFrom":makeQuery(id+"F35.opExtrude","SWEPT_EDGE",EDGE,{"disambiguationData":[OSD([sQuery(id+"F8.wireOp",EDGE,"E4.right"),sQuery(id+"F34.wireOp",EDGE,"E70.top"),sQuery(id+"F34.wireOp",EDGE,"E70.left")])]})});
            var Q8;
            Q8=makeQuery(id+"F9.opExtrude","SWEPT_EDGE",EDGE,{"disambiguationData":[OSD([sQuery(id+"F8.wireOp",EDGE,"E4.bottom"),sQuery(id+"F8.wireOp",EDGE,"E4.right")])]});
            var Q9;
            Q9=makeQuery(id+"F35.boolean.opBoolean","COPY",EDGE,{"derivedFrom":makeQuery(id+"F35.opExtrude","SWEPT_EDGE",EDGE,{"disambiguationData":[OSD([sQuery(id+"F34.wireOp",EDGE,"E72.top"),sQuery(id+"F34.wireOp",EDGE,"E72.left")])]})});
            var Q10;
            Q10=makeQuery(id+"F15.opExtrude","SWEPT_EDGE",EDGE,{"disambiguationData":[OSD([sQuery(id+"F14.wireOp",EDGE,"E8.top"),sQuery(id+"F14.wireOp",EDGE,"E8.left")])]});
            var Q11;
            {var subQ0=sQuery(id+"F0.wireOp",EDGE,"E0.top");Q11=makeQuery(id+"F29.opBoolean","SPLIT",EDGE,{"disambiguationData":[topologyDisambiguationEdgeConnected([makeQuery(id+"F15.opExtrude","SWEPT_FACE",FACE,{"disambiguationData":[OSD([sQuery(id+"F14.wireOp",EDGE,"E8.right")])]})])],"derivedFrom":makeQuery(id+"F1.opExtrude","SWEPT_EDGE",EDGE,{"disambiguationData":[OSD([subQ0,sQuery(id+"F0.wireOp",EDGE,"E0.left")])]})});}
            var Q12;
            Q12=makeQuery(id+"F17.opExtrude","SWEPT_EDGE",EDGE,{"disambiguationData":[OSD([sQuery(id+"F14.wireOp",EDGE,"E8.right"),sQuery(id+"F16.wireOp",EDGE,"E29"),sQuery(id+"F16.wireOp",EDGE,"E30")])]});
            var Q13;
            Q13=makeQuery(id+"F17.opExtrude","SWEPT_EDGE",EDGE,{"disambiguationData":[OSD([sQuery(id+"F16.wireOp",EDGE,"E27"),sQuery(id+"F16.wireOp",EDGE,"E28")])]});
            var Q14;
            Q14=makeQuery(id+"F15.opExtrude","SWEPT_EDGE",EDGE,{"disambiguationData":[OSD([sQuery(id+"F14.wireOp",EDGE,"E12.top"),sQuery(id+"F14.wireOp",EDGE,"E12.right")])]});
            var Q15;
            Q15=makeQuery(id+"F17.opExtrude","SWEPT_EDGE",EDGE,{"disambiguationData":[OSD([sQuery(id+"F14.wireOp",EDGE,"E12.top"),sQuery(id+"F14.wireOp",EDGE,"E12.right")])]});
            chamfer(context, id + "F36", {"entities" : qUnion([Q0, Q1, Q2, Q3, Q4, Q5, Q6, Q7, Q8, Q9, Q10, Q11, Q12, Q13, Q14, Q15]), "width" : 1.5 * mm, "tangentPropagation" : true});
        }
        {
            var Q0;
            {var subQ0=sQuery(id+"F5.wireOp",EDGE,"E3.left");Q0=makeQuery(id+"F7.opShell","OFFSET_EDGE",EDGE,{"disambiguationData":[OSD([subQ0]),TDD([makeQuery(id+"F6.opExtrude","CAP_EDGE",EDGE,{"disambiguationData":[OSD([subQ0])],"isStart":false})])]});}
            chamfer(context, id + "F37", {"entities" : qUnion([Q0]), "width" : 1.5 * mm, "tangentPropagation" : true});
        }
    });
